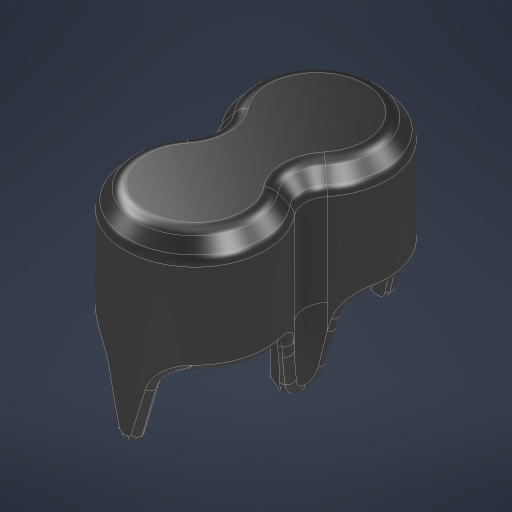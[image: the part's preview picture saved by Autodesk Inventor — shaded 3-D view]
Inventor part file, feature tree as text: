
AUTODESK INVENTOR PART (.ipt)
format: ipt  version: 2024 (Build 280153000, 153)  size: 830,464 bytes
history: native  units: mm
features: fillet x12, sketch x8, extrude x7, draft x4, chamfer x3, mirror x2, plane x2
ambient origin geometry x8: Origin, YZ Plane, XZ Plane, XY Plane, X Axis, Y Axis, Z Axis, Center Point
bodies: Solid1 (feature_tree)
feature tree (38):
  extrude  "Extrusion1"  Depth=23.0mm
  extrude  "Extrusion2"  Depth=27.0mm
  fillet  "Fillet1"  Radius=27.0mm
  extrude  "Extrusion3"  Depth=23.0mm
  fillet  "Fillet4"  [1 undecoded]
  extrude  "Extrusion4"  Depth=5.0mm
  extrude  "Extrusion5"  Depth=7.0mm
  extrude  "Extrusion9"  Depth=20.0mm TaperAngle=0.0deg
  mirror  "Mirror1"
  draft  "FaceDraft1"
  draft  "FaceDraft2"
  draft  "FaceDraft3"
  draft  "FaceDraft4"
  fillet  "Fillet8"  Radius=0.75mm
  fillet  "Fillet9"  Radius=23.0mm
  fillet  "Fillet10"  [1 undecoded]
  fillet  "Fillet11"  Radius=21.0mm
  fillet  "Fillet12"  Radius=21.0mm
  chamfer  "Chamfer1"  Distance=3.0mm
  extrude  "Extrusion14"  Depth=1.0mm
  chamfer  "Chamfer2"  Distance=3.0mm
  chamfer  "Chamfer3"  Distance=14.0mm
  fillet  "Fillet13"  [1 undecoded]
  fillet  "Fillet14"  [1 undecoded]
  fillet  "Fillet15"  [1 undecoded]
  sketch  "Sketch15"  dims[d61=4.25mm d62=1.25mm d63=1.25mm d64=1.25mm d95=3.0mm d96=2.0mm d97=8.726646mm d100=14.0mm d101=7.0mm d102=0.0mm d103=0.0mm d104=15.0mm d105=2.0mm d106=2.443461mm d107=15.0mm d108=2.0mm d109=2.443461mm d110=5.75mm d111=1.5mm d112=1.0mm d113=-23.3mm d114=-11.65mm d115=2.5mm d116=2.5mm d13=0.0mm d30=0.0mm d31=0.0mm d32=0.0mm d33=0.0mm]
  plane  "Work Plane1"
  plane  "Work Plane2"
  mirror  "Mirror2"
  fillet  "Fillet16"  [1 undecoded]
  fillet  "Fillet17"  Radius=4.25mm
  sketch  "Sketch1"  dims[d0=23.0mm d1=23.0mm]
  sketch  "Sketch2"  dims[d2=0.3mm d3=27.0mm d4=27.0mm]
  sketch  "Sketch3"  dims[d5=22.0mm d6=0.0mm d7=23.0mm d8=0.0mm]
  sketch  "Sketch4"  dims[d9=2.0mm d10=0.0mm d11=5.0mm]
  sketch  "Sketch5"  dims[d14=23.0mm d15=7.0mm]
  sketch  "Sketch9"  dims[d16=7.0mm d17=20.0mm d18=0.0mm d19=0.75mm d20=23.0mm d21=0.0mm d22=21.0mm d23=21.0mm d24=3.0mm d25=0.0mm]
  sketch  "Sketch14"  dims[d26=1.0mm d27=1.0mm d28=3.0mm d29=0.0mm d54=14.0mm d55=0.0mm d56=15.0deg d57=15.0deg d58=15.0deg d59=15.0deg d60=4.25mm]
note: 6 required parameter values undecoded (feature->parameter linkage not recoverable at this tier; creation-order binding heuristic only, values carry confidence <= 0.55)
